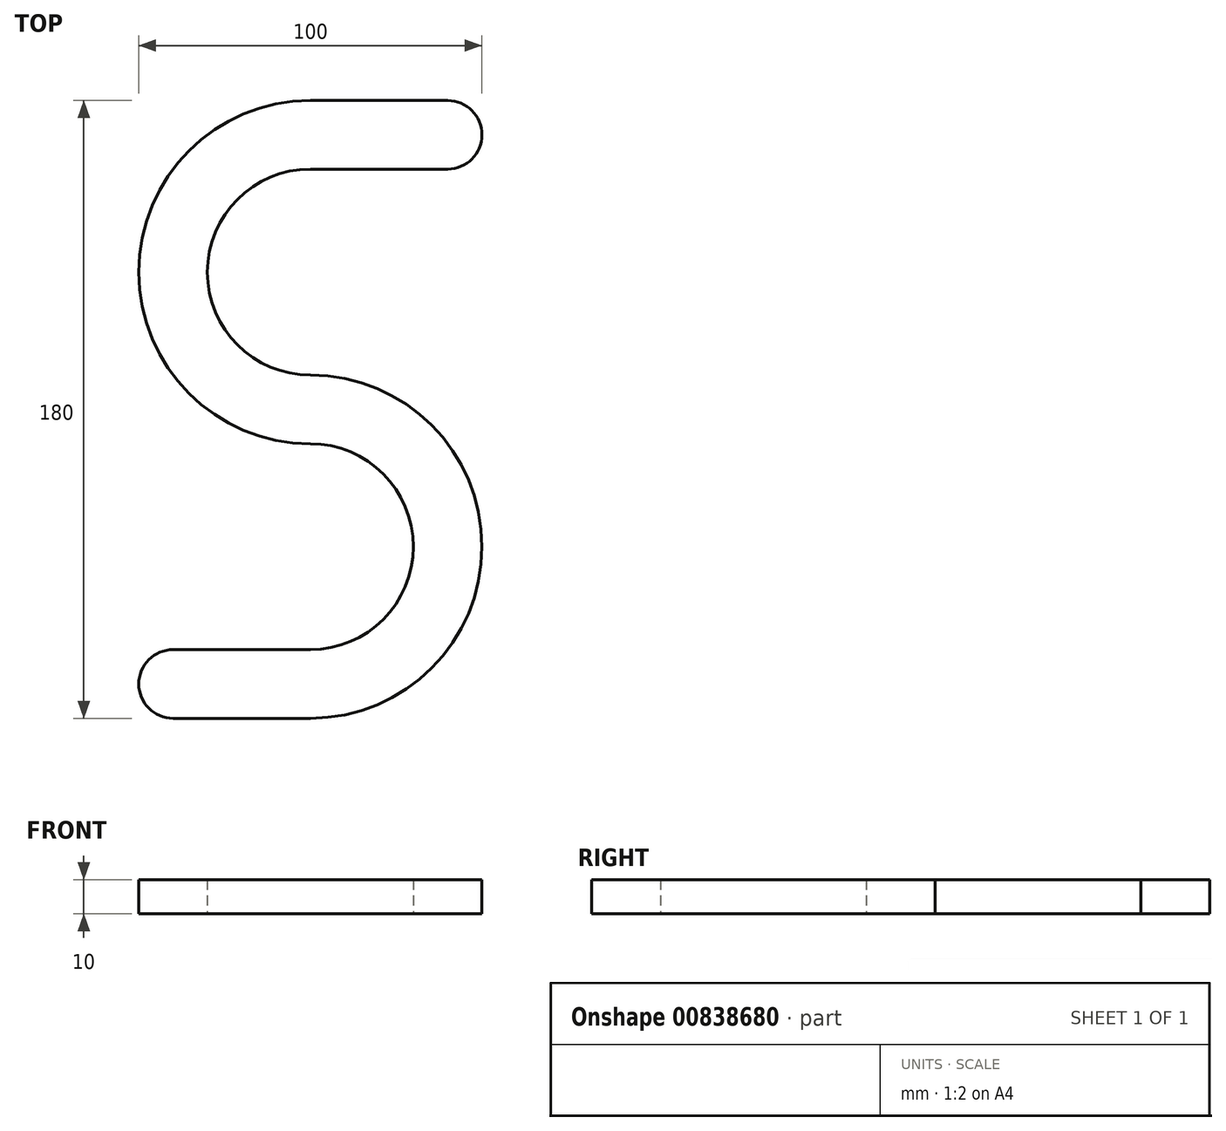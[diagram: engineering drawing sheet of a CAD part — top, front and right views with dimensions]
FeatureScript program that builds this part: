
annotation { "Feature Type Name" : "Feature", "Feature Type Description" : "" }
export const myFeature = defineFeature(function(context is Context, id is Id, definition is map)
    precondition{}
    {
        {
            var Q0;
            Q0=qCreatedBy(makeId("Top.planeOp"),FACE);
            var sketch = newSketch(context, id + "F0", { "sketchPlane" : qUnion([Q0])});
            skArc(sketch, "E0", {"start": v(0, 90) * mm, "mid": v(-50, 40) * mm, "end": v(0, -10) * mm});
            skArc(sketch, "E1", {"start": v(0, -70) * mm, "mid": v(30, -40) * mm, "end": v(0, -10) * mm});
            skArc(sketch, "E2", {"start": v(0, 70) * mm, "mid": v(-30, 40) * mm, "end": v(0, 10) * mm});
            skArc(sketch, "E3", {"start": v(40, 70) * mm, "mid": v(50, 80) * mm, "end": v(40, 90) * mm});
            skPoint(sketch, "E4", {"position": v(50, -40) * mm});
            skPoint(sketch, "E5", {"position": v(-50, 40) * mm});
            skPoint(sketch, "E6", {"position": v(50, 80) * mm});
            skArc(sketch, "E7", {"start": v(-40, -70) * mm, "mid": v(-50, -80) * mm, "end": v(-40, -90) * mm});
            skPoint(sketch, "E8", {"position": v(-50, -80) * mm});
            skLineSegment(sketch, "E9", {"start": v(0, 90) * mm, "end": v(40, 90) * mm});
            skLineSegment(sketch, "E10", {"start": v(0, 70) * mm, "end": v(40, 70) * mm});
            skLineSegment(sketch, "E11", {"start": v(0, -70) * mm, "end": v(-40, -70) * mm});
            skLineSegment(sketch, "E12", {"start": v(0, -90) * mm, "end": v(-40, -90) * mm});
            skArc(sketch, "E13.trimOffspring", {"start": v(0, -90) * mm, "mid": v(50, -40) * mm, "end": v(0, 10) * mm});
            skSolve(sketch);
        }
        {
            var Q0;
            Q0=makeQuery(id+"F0.imprint","IMPRINT",FACE,{"disambiguationData":[TD([[makeQuery(id+"F0.imprint","IMPRINT",EDGE,{"derivedFrom":sQuery(id+"F0.wireOp",EDGE,"E0")}),1.0]])]});
            extrude(context, id + "F1", {"entities" : qUnion([Q0]), "depth" : 10 * mm, "offsetDistance" : 25 * mm});
        }
    });
